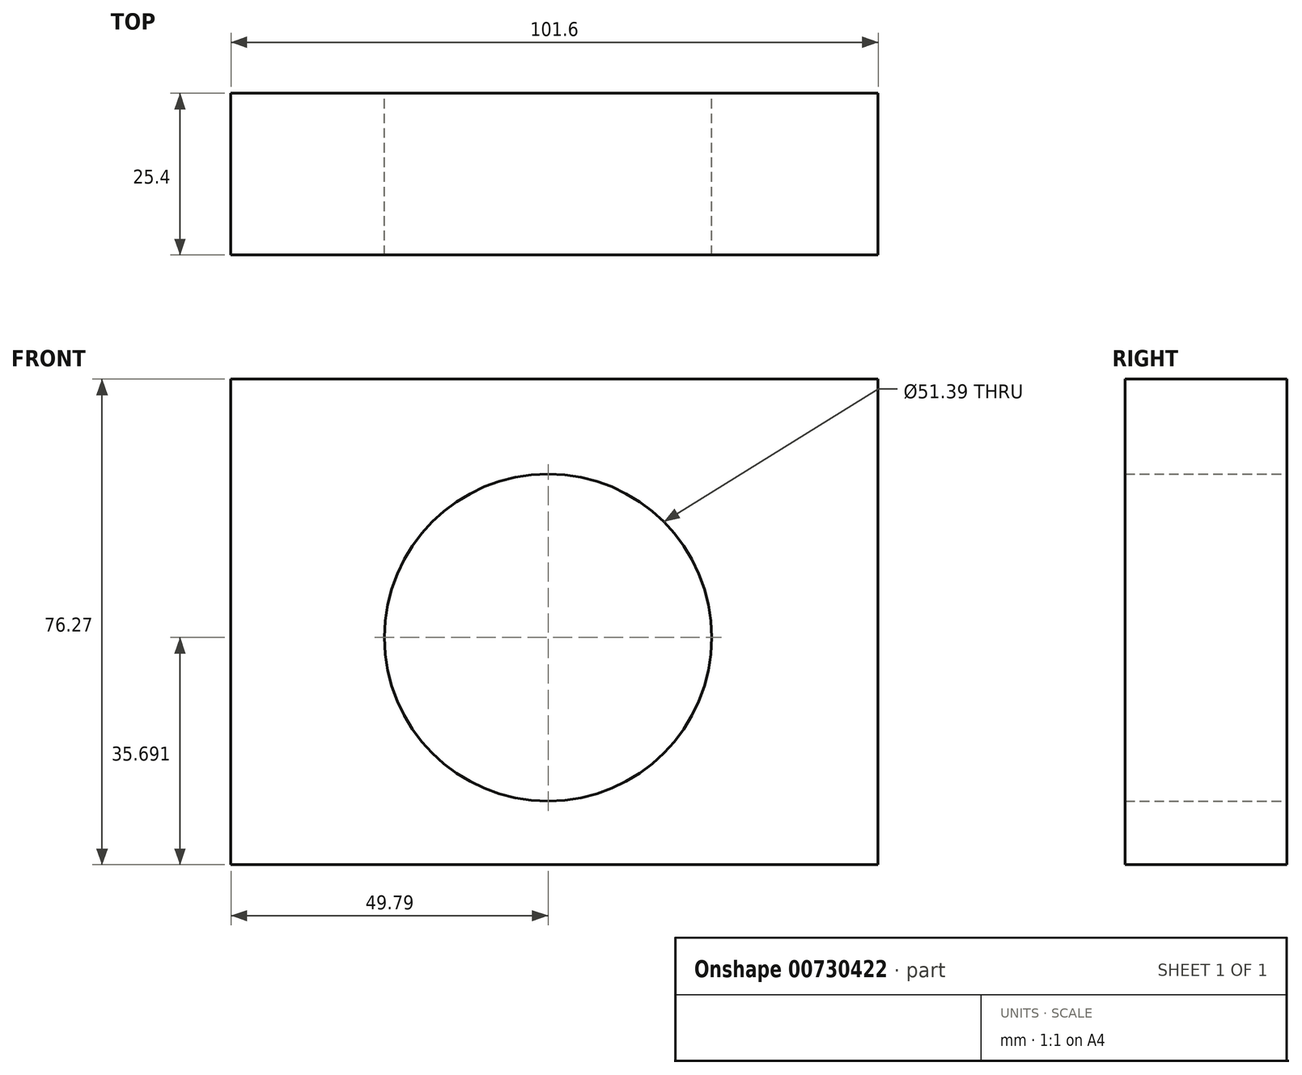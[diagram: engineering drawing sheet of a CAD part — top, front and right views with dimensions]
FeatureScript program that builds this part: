
annotation { "Feature Type Name" : "Feature", "Feature Type Description" : "" }
export const myFeature = defineFeature(function(context is Context, id is Id, definition is map)
    precondition{}
    {
        {
            var Q0;
            Q0=qCreatedBy(makeId("Front.planeOp"),FACE);
            var sketch = newSketch(context, id + "F0", { "sketchPlane" : qUnion([Q0])});
            skLineSegment(sketch, "E0.bottom", {"start": v(-55.7, 47.63) * mm, "end": v(45.9, 47.63) * mm});
            skLineSegment(sketch, "E0.top", {"start": v(-55.7, -28.64) * mm, "end": v(45.9, -28.64) * mm});
            skLineSegment(sketch, "E0.left", {"start": v(-55.7, 47.63) * mm, "end": v(-55.7, -28.64) * mm});
            skLineSegment(sketch, "E0.right", {"start": v(45.9, 47.63) * mm, "end": v(45.9, -28.64) * mm});
            skSolve(sketch);
        }
        {
            var Q0;
            Q0=makeQuery(id+"F0.imprint","IMPRINT",FACE,{"disambiguationData":[TD([[makeQuery(id+"F0.imprint","IMPRINT",EDGE,{"derivedFrom":sQuery(id+"F0.wireOp",EDGE,"E0.bottom")}),-1.0]])]});
            var sketch = newSketch(context, id + "F1", { "sketchPlane" : qUnion([Q0])});
            skCircle(sketch, "E1", {"center": v(-5.9, 7.05) * mm, "radius": 25.7 * mm});
            skSolve(sketch);
        }
        {
            var Q0;
            Q0=makeQuery(id+"F1.imprint","IMPRINT",FACE,{"disambiguationData":[TD([[makeQuery(id+"F1.imprint","IMPRINT",EDGE,{"derivedFrom":sQuery(id+"F1.wireOp",EDGE,"E1")}),-1.0]])]});
            extrude(context, id + "F2", {"entities" : qUnion([Q0]), "depth" : 25.4 * mm, "offsetDistance" : 25.4 * mm});
        }
    });
